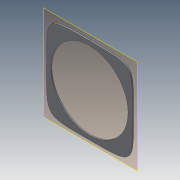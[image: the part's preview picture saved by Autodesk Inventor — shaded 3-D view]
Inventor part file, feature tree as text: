
AUTODESK INVENTOR PART (.ipt)
format: ipt  version: 2014 SP1 (Build 180222100, 222)  size: 106,496 bytes
history: native  units: in
note: dims shown in document units (in); Inventor stores cm internally (conversion verified against a paired STEP export)
features: reference x8, plane x1, extrude x1, other x1, sketch x1
ambient origin geometry x8: Origin, YZ Plane, XZ Plane, XY Plane, X Axis, Y Axis, Z Axis, Center Point
bodies: Solid1 (feature_tree)
feature tree (12):
  plane  "Work Plane1"
  extrude  "Extrusion1"  Depth=5.0in
  other  "Work Axis1"
  sketch  "Sketch1"  dims[d0=5.0in d1=5.0in d2=2.5in d3=2.5in d4=6.75in d5=0.1083in d6=0.0in]
  reference  "Reference1"
  reference  "Reference2"
  reference  "Reference3"
  reference  "Reference4"
  reference  "Reference5"
  reference  "Reference6"
  reference  "Reference7"
  reference  "Reference8"
